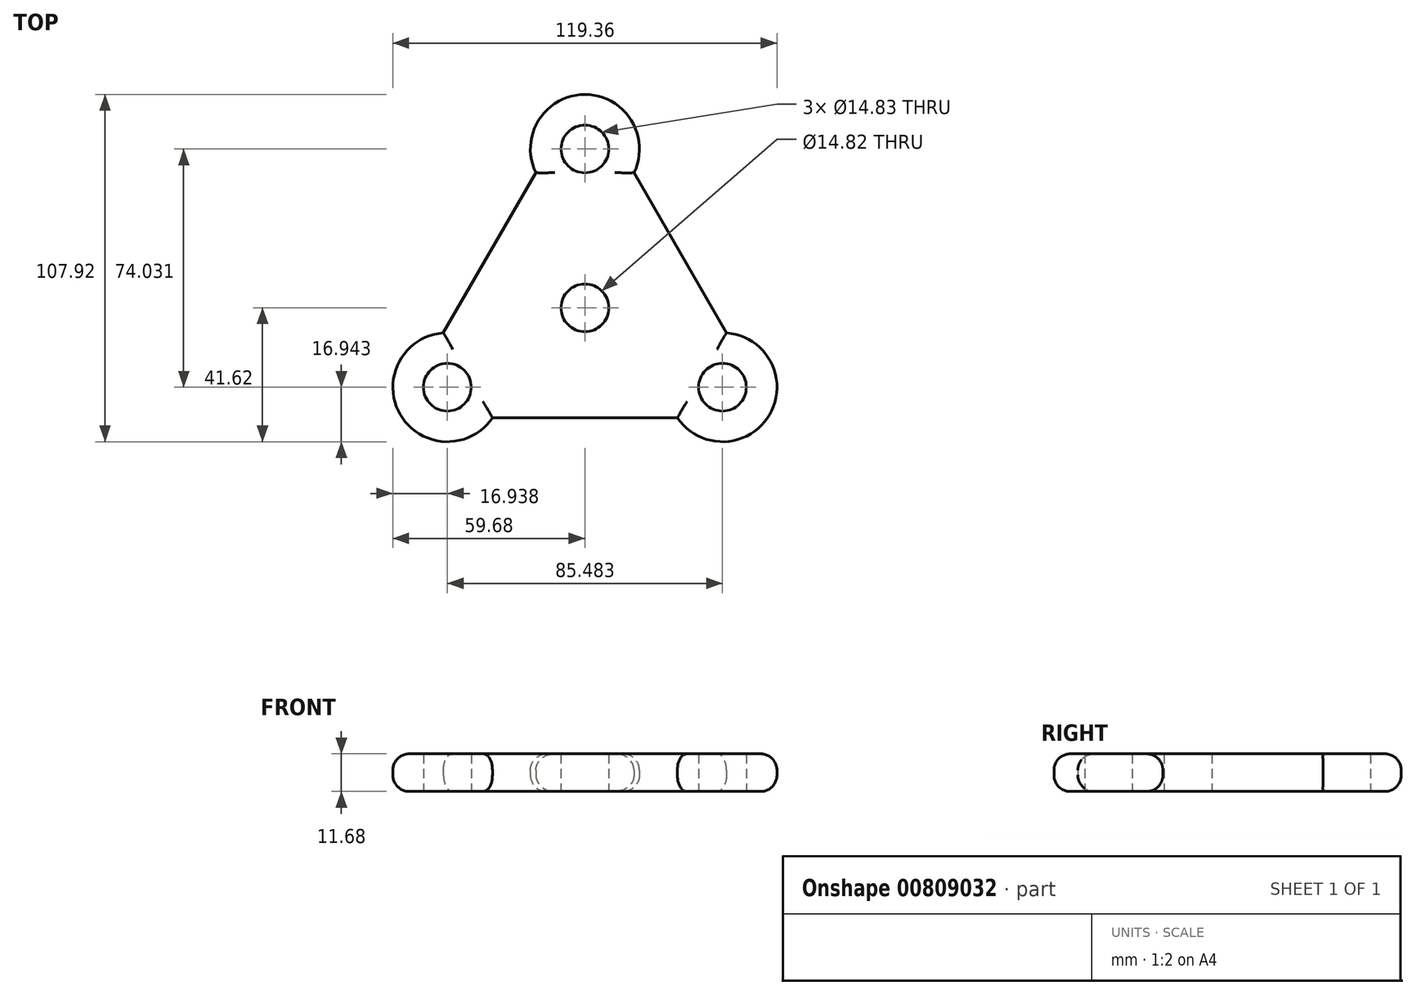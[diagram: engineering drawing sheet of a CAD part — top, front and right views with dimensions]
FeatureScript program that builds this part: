
annotation { "Feature Type Name" : "Feature", "Feature Type Description" : "" }
export const myFeature = defineFeature(function(context is Context, id is Id, definition is map)
    precondition{}
    {
        {
            var Q0;
            Q0=qCreatedBy(makeId("Top.planeOp"),FACE);
            var sketch = newSketch(context, id + "F0", { "sketchPlane" : qUnion([Q0])});
            skCircle(sketch, "E0", {"center": v(0, 0) * mm, "radius": 7.41 * mm});
            skCircle(sketch, "E1.cCircle", {"center": v(0, 0) * mm, "radius": 24.68 * mm, "construction": true});
            skLineSegment(sketch, "E1.0", {"start": v(-39.03, -18.25) * mm, "end": v(-3.7, 42.93) * mm});
            skLineSegment(sketch, "E1.1", {"start": v(0, 49.35) * mm, "end": v(0.53, 48.43) * mm});
            skLineSegment(sketch, "E1.2", {"start": v(35.32, -24.68) * mm, "end": v(-35.32, -24.68) * mm});
            skPoint(sketch, "E1.0.midPoint", {"position": v(-21.37, 12.34) * mm});
            skCircle(sketch, "E2", {"center": v(0, 49.35) * mm, "radius": 7.42 * mm});
            skCircle(sketch, "E3", {"center": v(42.74, -24.68) * mm, "radius": 7.42 * mm});
            skCircle(sketch, "E4", {"center": v(-42.74, -24.68) * mm, "radius": 7.42 * mm});
            skLineSegment(sketch, "E5.0", {"start": v(-43.99, -7.78) * mm, "end": v(-15.25, 41.98) * mm});
            skLineSegment(sketch, "E5.1", {"start": v(28.73, -34.2) * mm, "end": v(-28.73, -34.2) * mm});
            skLineSegment(sketch, "E5.2", {"start": v(15.25, 41.98) * mm, "end": v(43.99, -7.78) * mm});
            skCircle(sketch, "E6.0", {"center": v(0, 49.35) * mm, "radius": 1.07 * mm});
            skArc(sketch, "E7.0", {"start": v(-43.99, -7.78) * mm, "mid": v(-57.41, -33.15) * mm, "end": v(-28.73, -34.2) * mm});
            skArc(sketch, "E8.0", {"start": v(15.25, 41.98) * mm, "mid": v(0, 66.3) * mm, "end": v(-15.25, 41.98) * mm});
            skArc(sketch, "E9.0", {"start": v(28.73, -34.2) * mm, "mid": v(57.41, -33.15) * mm, "end": v(43.99, -7.78) * mm});
            skLineSegment(sketch, "E10.trimOffspring", {"start": v(3.7, 42.93) * mm, "end": v(39.03, -18.25) * mm});
            skLineSegment(sketch, "E11.trimOffspring", {"start": v(-0.53, 48.43) * mm, "end": v(0, 49.35) * mm});
            skSolve(sketch);
        }
        {
            var Q0;
            {var subQ1=sQuery(id+"F0.wireOp",EDGE,"E1.0");Q0=makeQuery(id+"F0.imprint","IMPRINT",FACE,{"disambiguationData":[TD([[makeQuery(id+"F0.imprint","IMPRINT",EDGE,{"derivedFrom":subQ1}),1.0]])]});}
            var Q1;
            Q1=makeQuery(id+"F0.imprint","IMPRINT",FACE,{"disambiguationData":[TD([[makeQuery(id+"F0.imprint","IMPRINT",EDGE,{"derivedFrom":sQuery(id+"F0.wireOp",EDGE,"E0")}),-1.0]])]});
            extrude(context, id + "F1", {"entities" : qUnion([Q0, Q1]), "depth" : 11.68 * mm, "offsetDistance" : 25.4 * mm});
        }
        {
            var Q0;
            Q0=makeQuery(id+"F1.opExtrude","CAP_EDGE",EDGE,{"disambiguationData":[OSD([sQuery(id+"F0.wireOp",EDGE,"E5.1")])],"isStart":true});
            var Q1;
            Q1=makeQuery(id+"F1.opExtrude","CAP_EDGE",EDGE,{"disambiguationData":[OSD([sQuery(id+"F0.wireOp",EDGE,"E5.1")])],"isStart":false});
            var Q2;
            Q2=makeQuery(id+"F1.opExtrude","CAP_EDGE",EDGE,{"disambiguationData":[OSD([sQuery(id+"F0.wireOp",EDGE,"E9.0")])],"isStart":false});
            var Q3;
            Q3=makeQuery(id+"F1.opExtrude","CAP_EDGE",EDGE,{"disambiguationData":[OSD([sQuery(id+"F0.wireOp",EDGE,"E7.0")])],"isStart":false});
            var Q4;
            Q4=makeQuery(id+"F1.opExtrude","CAP_EDGE",EDGE,{"disambiguationData":[OSD([sQuery(id+"F0.wireOp",EDGE,"E5.0")])],"isStart":false});
            var Q5;
            Q5=makeQuery(id+"F1.opExtrude","CAP_EDGE",EDGE,{"disambiguationData":[OSD([sQuery(id+"F0.wireOp",EDGE,"E8.0")])],"isStart":false});
            var Q6;
            Q6=makeQuery(id+"F1.opExtrude","CAP_EDGE",EDGE,{"disambiguationData":[OSD([sQuery(id+"F0.wireOp",EDGE,"E5.2")])],"isStart":true});
            var Q7;
            Q7=makeQuery(id+"F1.opExtrude","CAP_EDGE",EDGE,{"disambiguationData":[OSD([sQuery(id+"F0.wireOp",EDGE,"E5.2")])],"isStart":false});
            var Q8;
            Q8=makeQuery(id+"F1.opExtrude","CAP_EDGE",EDGE,{"disambiguationData":[OSD([sQuery(id+"F0.wireOp",EDGE,"E9.0")])],"isStart":true});
            var Q9;
            Q9=makeQuery(id+"F1.opExtrude","CAP_EDGE",EDGE,{"disambiguationData":[OSD([sQuery(id+"F0.wireOp",EDGE,"E7.0")])],"isStart":true});
            var Q10;
            Q10=makeQuery(id+"F1.opExtrude","CAP_EDGE",EDGE,{"disambiguationData":[OSD([sQuery(id+"F0.wireOp",EDGE,"E8.0")])],"isStart":true});
            var Q11;
            Q11=makeQuery(id+"F1.opExtrude","CAP_EDGE",EDGE,{"disambiguationData":[OSD([sQuery(id+"F0.wireOp",EDGE,"E5.0")])],"isStart":true});
            fillet(context, id + "F2", {"entities" : qUnion([Q0, Q1, Q2, Q3, Q4, Q5, Q6, Q7, Q8, Q9, Q10, Q11]), "radius" : 5.08 * mm, "tangentPropagation" : true, "allowEdgeOverflow" : false});
        }
    });
